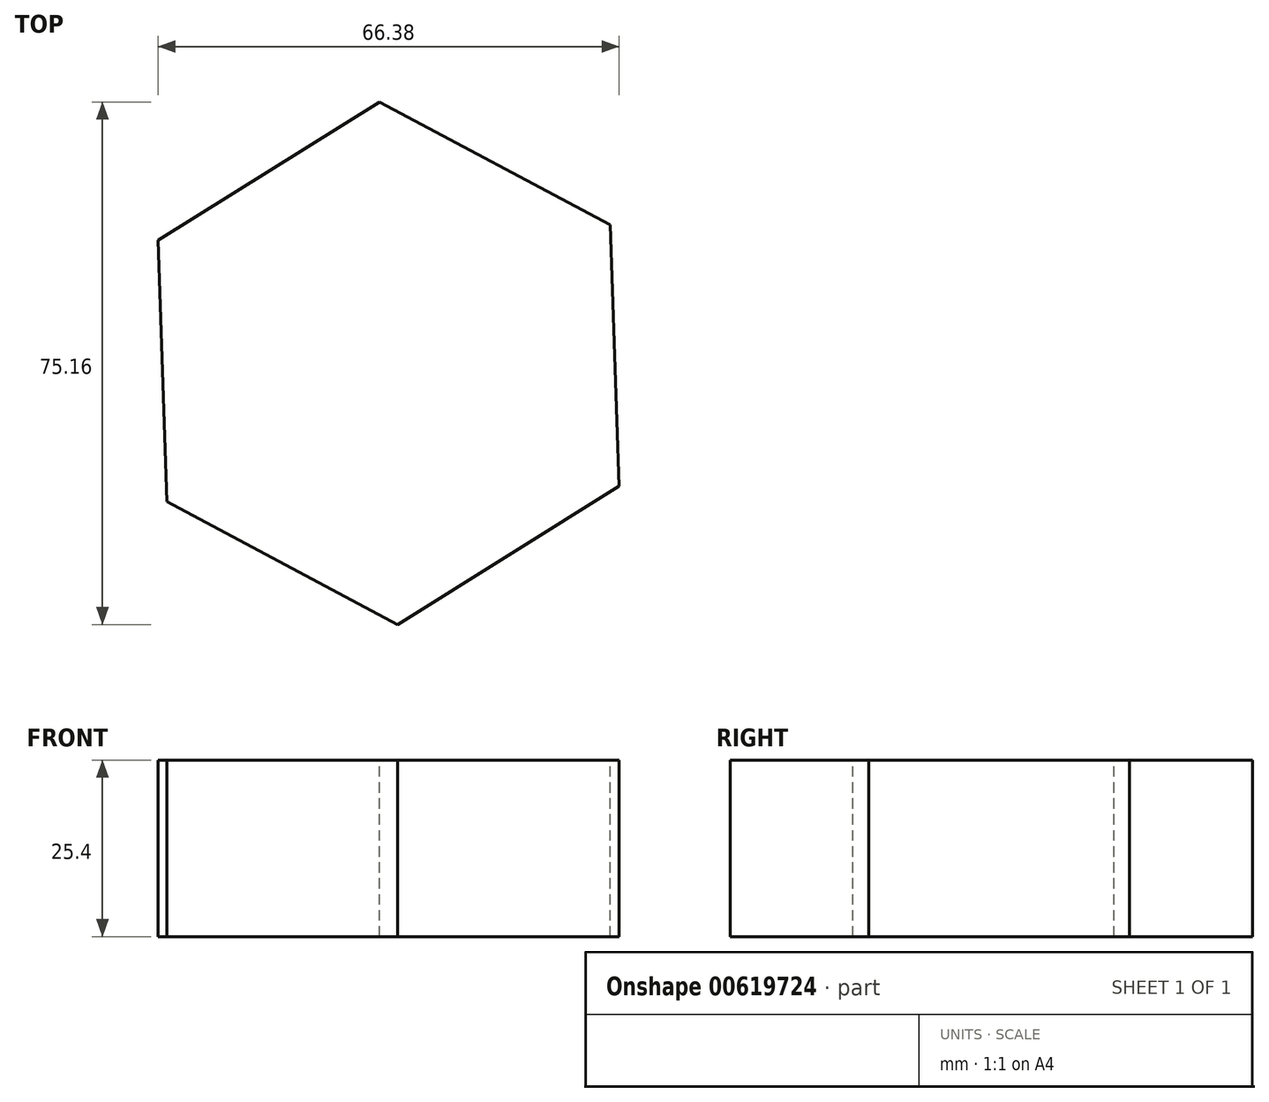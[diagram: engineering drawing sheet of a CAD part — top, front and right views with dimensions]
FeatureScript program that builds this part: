
annotation { "Feature Type Name" : "Feature", "Feature Type Description" : "" }
export const myFeature = defineFeature(function(context is Context, id is Id, definition is map)
    precondition{}
    {
        {
            var Q0;
            Q0=qCreatedBy(makeId("Top.planeOp"),FACE);
            var sketch = newSketch(context, id + "F0", { "sketchPlane" : qUnion([Q0])});
            skCircle(sketch, "E0.cCircle", {"center": v(0, 0) * mm, "radius": 32.56 * mm, "construction": true});
            skLineSegment(sketch, "E0.0", {"start": v(-33.19, 17.68) * mm, "end": v(-1.29, 37.58) * mm});
            skLineSegment(sketch, "E0.1", {"start": v(-1.29, 37.58) * mm, "end": v(31.9, 19.9) * mm});
            skLineSegment(sketch, "E0.2", {"start": v(31.9, 19.9) * mm, "end": v(33.19, -17.68) * mm});
            skLineSegment(sketch, "E0.3", {"start": v(33.19, -17.68) * mm, "end": v(1.29, -37.58) * mm});
            skLineSegment(sketch, "E0.4", {"start": v(1.29, -37.58) * mm, "end": v(-31.9, -19.9) * mm});
            skLineSegment(sketch, "E0.5", {"start": v(-31.9, -19.9) * mm, "end": v(-33.19, 17.68) * mm});
            skPoint(sketch, "E0.0.midPoint", {"position": v(-17.24, 27.63) * mm});
            skSolve(sketch);
        }
        {
            var Q0;
            Q0=sQuery(id+"F0.wireOp",EDGE,"E0.5");
            var Q1;
            Q1=sQuery(id+"F0.wireOp",EDGE,"E0.0");
            var Q2;
            Q2=sQuery(id+"F0.wireOp",EDGE,"E0.1");
            var Q3;
            Q3=sQuery(id+"F0.wireOp",EDGE,"E0.2");
            var Q4;
            Q4=sQuery(id+"F0.wireOp",EDGE,"E0.3");
            var Q5;
            Q5=sQuery(id+"F0.wireOp",EDGE,"E0.4");
            extrude(context, id + "F1", {"bodyType" : ToolBodyType.SURFACE, "surfaceEntities" : qUnion([Q0, Q1, Q2, Q3, Q4, Q5]), "depth" : 25.4 * mm, "offsetDistance" : 25.4 * mm});
        }
    });
